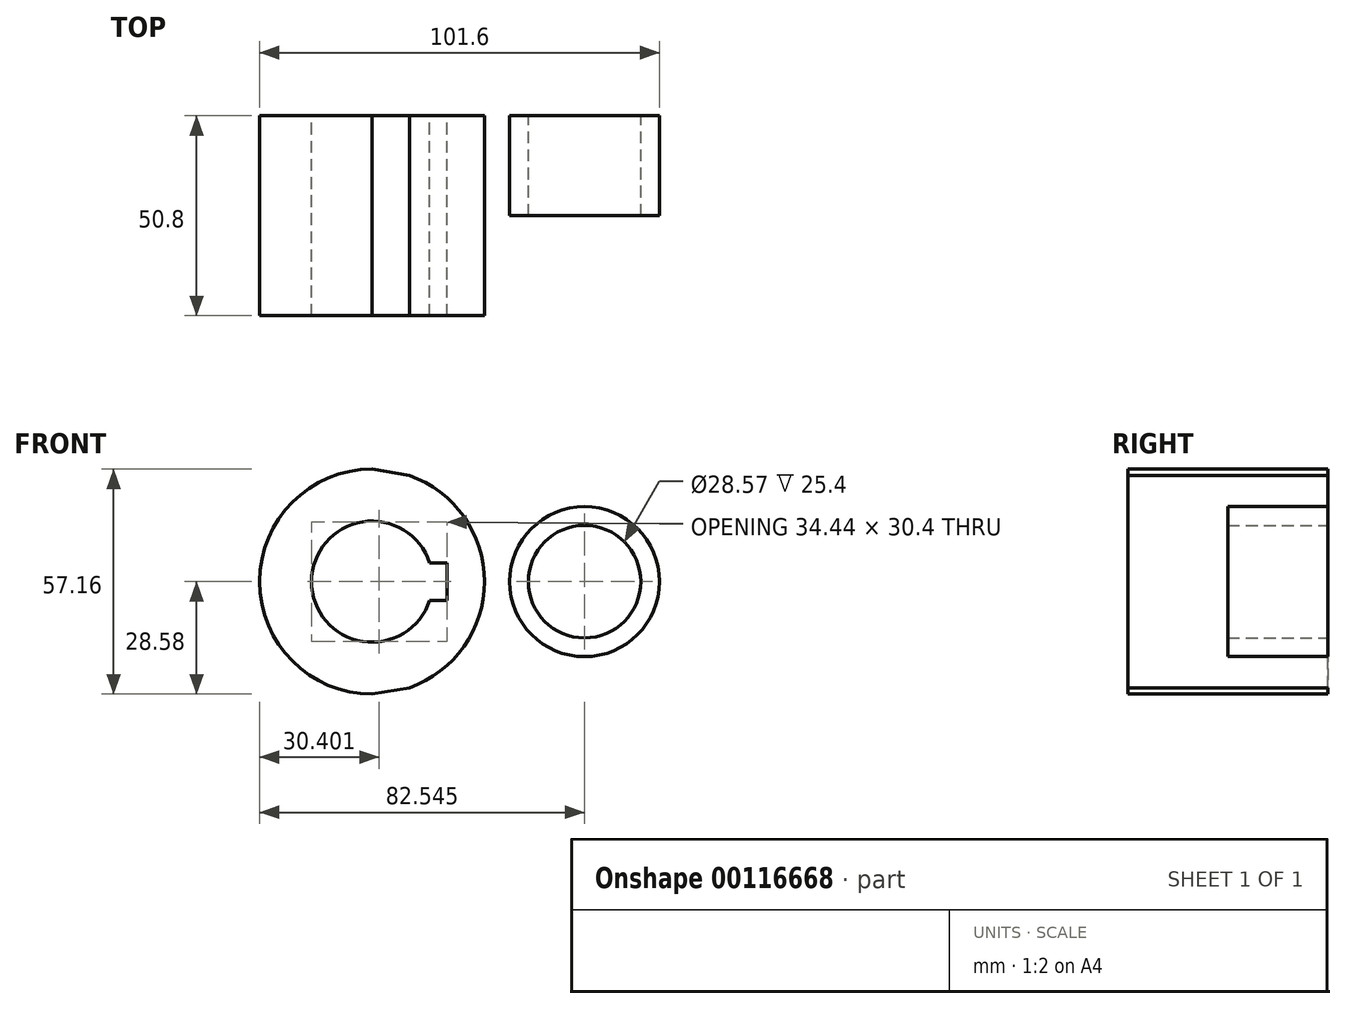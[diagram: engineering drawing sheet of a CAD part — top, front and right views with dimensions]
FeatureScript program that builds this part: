
annotation { "Feature Type Name" : "Feature", "Feature Type Description" : "" }
export const myFeature = defineFeature(function(context is Context, id is Id, definition is map)
    precondition{}
    {
        {
            var Q0;
            Q0=qCreatedBy(makeId("Front.planeOp"),FACE);
            var sketch = newSketch(context, id + "F0", { "sketchPlane" : qUnion([Q0])});
            skCircle(sketch, "E0", {"center": v(0, 0) * mm, "radius": 28.58 * mm});
            skCircle(sketch, "E1", {"center": v(53.97, 0) * mm, "radius": 19.05 * mm});
            skLineSegment(sketch, "E2", {"start": v(0, 28.58) * mm, "end": v(57.2, 18.78) * mm});
            skLineSegment(sketch, "E3", {"start": v(0, -28.58) * mm, "end": v(57.2, -18.78) * mm});
            skCircle(sketch, "E4", {"center": v(53.97, 0) * mm, "radius": 14.29 * mm});
            skCircle(sketch, "E5", {"center": v(0, 0) * mm, "radius": 15.39 * mm});
            skLineSegment(sketch, "E6.bottom", {"start": v(-19.05, 4.76) * mm, "end": v(19.05, 4.76) * mm});
            skLineSegment(sketch, "E6.top", {"start": v(-19.05, -4.76) * mm, "end": v(19.05, -4.76) * mm});
            skLineSegment(sketch, "E6.left", {"start": v(-19.05, 4.76) * mm, "end": v(-19.05, -4.76) * mm});
            skLineSegment(sketch, "E6.right", {"start": v(19.05, 4.76) * mm, "end": v(19.05, -4.76) * mm});
            skSolve(sketch);
        }
        {
            var Q0;
            {var subQ5=sQuery(id+"F0.wireOp",EDGE,"E6.left");Q0=makeQuery(id+"F0.imprint","IMPRINT",FACE,{"disambiguationData":[TD([[makeQuery(id+"F0.imprint","IMPRINT",EDGE,{"derivedFrom":subQ5}),-1.0]])]});}
            var Q1;
            {var subQ5=sQuery(id+"F0.wireOp",EDGE,"E6.left");Q1=makeQuery(id+"F0.imprint","IMPRINT",FACE,{"disambiguationData":[TD([[makeQuery(id+"F0.imprint","IMPRINT",EDGE,{"derivedFrom":subQ5}),1.0]])]});}
            var Q2;
            {var subQ0=sQuery(id+"F0.wireOp",EDGE,"E2");var subQ1=sQuery(id+"F0.wireOp",EDGE,"E0");var subQ2=makeQuery(id+"F0.imprint","INTERSECT",VERTEX,{"disambiguationData":[OD(1.0)],"derivedFrom":[subQ1,subQ0]});Q2=makeQuery(id+"F0.imprint","IMPRINT",FACE,{"disambiguationData":[TD([[makeQuery(id+"F0.imprint","IMPRINT",EDGE,{"disambiguationData":[TD([[subQ2,1.0]])],"derivedFrom":subQ1}),-1.0]])]});}
            var Q3;
            Q3=makeQuery(id+"F0.imprint","IMPRINT",FACE,{"disambiguationData":[TD([[makeQuery(id+"F0.imprint","IMPRINT",EDGE,{"derivedFrom":sQuery(id+"F0.wireOp",EDGE,"E4")}),-1.0]])]});
            extrude(context, id + "F1", {"entities" : qUnion([Q0, Q1, Q2, Q3]), "depth" : 25.4 * mm});
        }
        {
            var Q0;
            {var subQ5=sQuery(id+"F0.wireOp",EDGE,"E6.left");Q0=makeQuery(id+"F0.imprint","IMPRINT",FACE,{"disambiguationData":[TD([[makeQuery(id+"F0.imprint","IMPRINT",EDGE,{"derivedFrom":subQ5}),-1.0]])]});}
            var Q1;
            {var subQ5=sQuery(id+"F0.wireOp",EDGE,"E6.left");Q1=makeQuery(id+"F0.imprint","IMPRINT",FACE,{"disambiguationData":[TD([[makeQuery(id+"F0.imprint","IMPRINT",EDGE,{"derivedFrom":subQ5}),1.0]])]});}
            extrude(context, id + "F2", {"entities" : qUnion([Q0, Q1]), "operationType" : NewBodyOperationType.ADD, "depth" : 50.8 * mm});
        }
    });
